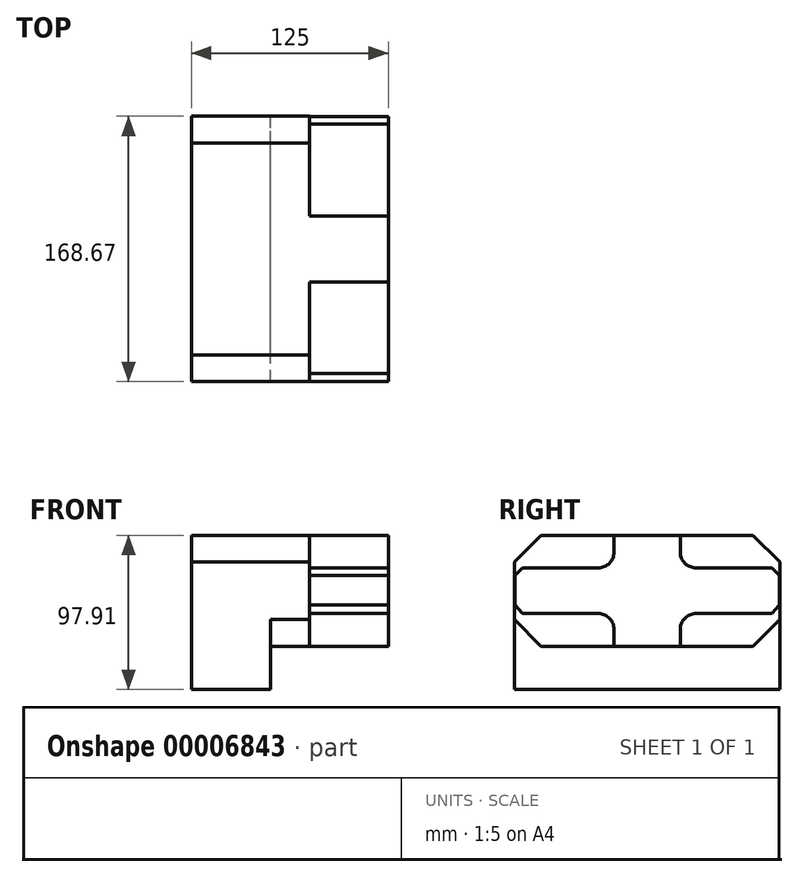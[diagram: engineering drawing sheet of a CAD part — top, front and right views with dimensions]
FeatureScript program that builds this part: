
annotation { "Feature Type Name" : "Feature", "Feature Type Description" : "" }
export const myFeature = defineFeature(function(context is Context, id is Id, definition is map)
    precondition{}
    {
        {
            var Q0;
            Q0=qCreatedBy(makeId("Right.planeOp"),FACE);
            var sketch = newSketch(context, id + "F0", { "sketchPlane" : qUnion([Q0])});
            skLineSegment(sketch, "E0.top", {"start": v(-12.5, 211.04) * mm, "end": v(122.19, 211.04) * mm, "construction": true});
            skLineSegment(sketch, "E0.left", {"start": v(-29.49, 113.13) * mm, "end": v(-29.49, 194.04) * mm, "construction": true});
            skLineSegment(sketch, "E0.right", {"start": v(139.18, 113.13) * mm, "end": v(139.18, 194.04) * mm, "construction": true});
            skLineSegment(sketch, "E1", {"start": v(-29.49, 113.13) * mm, "end": v(-29.49, 194.04) * mm});
            skLineSegment(sketch, "E2", {"start": v(-29.49, 194.04) * mm, "end": v(-12.5, 211.04) * mm});
            skLineSegment(sketch, "E3", {"start": v(-12.5, 211.04) * mm, "end": v(122.19, 211.04) * mm});
            skLineSegment(sketch, "E4", {"start": v(122.19, 211.04) * mm, "end": v(139.18, 194.04) * mm});
            skLineSegment(sketch, "E5", {"start": v(139.18, 194.04) * mm, "end": v(139.18, 113.13) * mm});
            skLineSegment(sketch, "E6", {"start": v(-29.49, 194.04) * mm, "end": v(-29.49, 211.04) * mm, "construction": true});
            skLineSegment(sketch, "E7", {"start": v(-29.49, 211.04) * mm, "end": v(-12.5, 211.04) * mm, "construction": true});
            skLineSegment(sketch, "E8", {"start": v(122.19, 211.04) * mm, "end": v(139.18, 211.04) * mm, "construction": true});
            skLineSegment(sketch, "E9", {"start": v(139.18, 211.04) * mm, "end": v(139.18, 194.04) * mm, "construction": true});
            skLineSegment(sketch, "E10", {"start": v(-29.49, 113.13) * mm, "end": v(139.18, 113.13) * mm});
            skSolve(sketch);
        }
        {
            var Q0;
            Q0 = qSketchRegion(id + "F0", true);
            extrude(context, id + "F1", {"entities" : qUnion([Q0]), "depth" : 50 * mm});
        }
        {
            var Q0;
            Q0=makeQuery(id+"F1.opExtrude","CAP_FACE",FACE,{"disambiguationData":[OSD([sQuery(id+"F0.wireOp",EDGE,"E1"),sQuery(id+"F0.wireOp",EDGE,"E2"),sQuery(id+"F0.wireOp",EDGE,"E3"),sQuery(id+"F0.wireOp",EDGE,"E4"),sQuery(id+"F0.wireOp",EDGE,"E5"),sQuery(id+"F0.wireOp",EDGE,"01fd04ff-37d6-47c2-a5c3-88bd0e4e2ab6"),sQuery(id+"F0.wireOp",EDGE,"aee49f88-fb62-4dc6-9d70-ac3d9b7b1557"),sQuery(id+"F0.wireOp",EDGE,"abb99656-4afa-4ae6-adc2-ed8c3525c0ab")])],"isStart":false});
            var sketch = newSketch(context, id + "F2", { "sketchPlane" : qUnion([Q0])});
            skLineSegment(sketch, "E11", {"start": v(-29.49, 194.04) * mm, "end": v(-12.5, 211.04) * mm});
            skLineSegment(sketch, "E12", {"start": v(-12.5, 211.04) * mm, "end": v(122.19, 211.04) * mm});
            skLineSegment(sketch, "E13", {"start": v(122.19, 211.04) * mm, "end": v(139.18, 194.04) * mm});
            skLineSegment(sketch, "E14", {"start": v(139.18, 194.04) * mm, "end": v(139.18, 157.51) * mm});
            skLineSegment(sketch, "E15", {"start": v(-29.49, 157.51) * mm, "end": v(-29.49, 194.04) * mm});
            skLineSegment(sketch, "E16", {"start": v(-29.49, 157.51) * mm, "end": v(-12.5, 140.51) * mm});
            skLineSegment(sketch, "E17", {"start": v(-12.5, 140.51) * mm, "end": v(122.19, 140.51) * mm});
            skLineSegment(sketch, "E18", {"start": v(122.19, 140.51) * mm, "end": v(139.18, 157.51) * mm});
            skSolve(sketch);
        }
        {
            var Q0;
            Q0 = qSketchRegion(id + "F2", true);
            extrude(context, id + "F3", {"entities" : qUnion([Q0]), "operationType" : NewBodyOperationType.ADD, "depth" : 25 * mm});
        }
        {
            var Q0;
            Q0=makeQuery(id+"F3.opExtrude","CAP_FACE",FACE,{"disambiguationData":[OSD([sQuery(id+"F2.wireOp",EDGE,"E11"),sQuery(id+"F2.wireOp",EDGE,"E12"),sQuery(id+"F2.wireOp",EDGE,"E13"),sQuery(id+"F2.wireOp",EDGE,"E14"),sQuery(id+"F2.wireOp",EDGE,"E15"),sQuery(id+"F2.wireOp",EDGE,"E16"),sQuery(id+"F2.wireOp",EDGE,"E17"),sQuery(id+"F2.wireOp",EDGE,"E18")])],"isStart":false});
            var sketch = newSketch(context, id + "F4", { "sketchPlane" : qUnion([Q0])});
            skLineSegment(sketch, "E19.bottom", {"start": v(75.9, 211.04) * mm, "end": v(33.8, 211.04) * mm});
            skLineSegment(sketch, "E19.top", {"start": v(75.9, 140.51) * mm, "end": v(33.8, 140.51) * mm});
            skLineSegment(sketch, "E19.left", {"start": v(75.9, 211.04) * mm, "end": v(75.9, 200.3) * mm});
            skLineSegment(sketch, "E19.right", {"start": v(33.8, 211.04) * mm, "end": v(33.8, 200.3) * mm});
            skPoint(sketch, "E20", {"position": v(54.85, 211.04) * mm});
            skPoint(sketch, "E21", {"position": v(33.8, 175.78) * mm});
            skLineSegment(sketch, "E22.bottom", {"start": v(23.8, 190.3) * mm, "end": v(-24.4, 190.3) * mm});
            skLineSegment(sketch, "E22.top", {"start": v(23.8, 161.25) * mm, "end": v(-24.4, 161.25) * mm});
            skLineSegment(sketch, "E22.right", {"start": v(-29.23, 185.47) * mm, "end": v(-29.23, 166.67) * mm});
            skPoint(sketch, "E23", {"position": v(75.9, 175.78) * mm});
            skLineSegment(sketch, "E24.bottom", {"start": v(134.1, 161.25) * mm, "end": v(85.9, 161.25) * mm});
            skLineSegment(sketch, "E24.top", {"start": v(134.1, 190.3) * mm, "end": v(85.9, 190.3) * mm});
            skLineSegment(sketch, "E24.left", {"start": v(138.93, 185.47) * mm, "end": v(138.93, 166.67) * mm});
            skLineSegment(sketch, "E25.trimOffspring", {"start": v(33.8, 151.25) * mm, "end": v(33.8, 140.51) * mm});
            skLineSegment(sketch, "E26.trimOffspring", {"start": v(75.9, 151.25) * mm, "end": v(75.9, 140.51) * mm});
            skLineSegment(sketch, "E27", {"start": v(-24.4, 190.3) * mm, "end": v(-29.23, 185.47) * mm});
            skLineSegment(sketch, "E28", {"start": v(-29.23, 166.67) * mm, "end": v(-24.4, 161.25) * mm});
            skLineSegment(sketch, "E29", {"start": v(134.1, 190.3) * mm, "end": v(138.93, 185.47) * mm});
            skLineSegment(sketch, "E30", {"start": v(138.93, 166.67) * mm, "end": v(134.1, 161.25) * mm});
            skPoint(sketch, "E31.orphan", {"position": v(138.93, 190.3) * mm});
            skLineSegment(sketch, "E32", {"start": v(134.1, 190.3) * mm, "end": v(134.1, 185.47) * mm, "construction": true});
            skLineSegment(sketch, "E33", {"start": v(134.1, 185.47) * mm, "end": v(138.93, 185.47) * mm, "construction": true});
            skLineSegment(sketch, "E34", {"start": v(-29.23, 185.47) * mm, "end": v(-24.4, 185.47) * mm, "construction": true});
            skLineSegment(sketch, "E35", {"start": v(-24.4, 185.47) * mm, "end": v(-24.4, 190.3) * mm, "construction": true});
            skPoint(sketch, "E36.visualSharp", {"position": v(33.8, 190.3) * mm});
            skArc(sketch, "E36.filletArc", {"start": v(23.8, 190.3) * mm, "mid": v(30.88, 193.23) * mm, "end": v(33.8, 200.3) * mm});
            skPoint(sketch, "E37.visualSharp", {"position": v(33.8, 161.25) * mm});
            skArc(sketch, "E37.filletArc", {"start": v(33.8, 151.25) * mm, "mid": v(30.88, 158.32) * mm, "end": v(23.8, 161.25) * mm});
            skPoint(sketch, "E38.visualSharp", {"position": v(75.9, 161.25) * mm});
            skArc(sketch, "E38.filletArc", {"start": v(85.9, 161.25) * mm, "mid": v(78.82, 158.32) * mm, "end": v(75.9, 151.25) * mm});
            skPoint(sketch, "E39.visualSharp", {"position": v(75.9, 190.3) * mm});
            skArc(sketch, "E39.filletArc", {"start": v(75.9, 200.3) * mm, "mid": v(78.82, 193.23) * mm, "end": v(85.9, 190.3) * mm});
            skSolve(sketch);
        }
        {
            var Q0;
            Q0 = qSketchRegion(id + "F4", true);
            extrude(context, id + "F5", {"entities" : qUnion([Q0]), "operationType" : NewBodyOperationType.ADD, "depth" : 50 * mm});
        }
    });
